# Revit family: 27435 PRESTO DL 400 E TOUCH
name_source: partatom
category: Appareils sanitaires
units: mm (PartAtom-declared; Revit-internal decimal feet)

## family parameters
Cote de connecteur circulaire = Utiliser le diamètre
Couper avec des vides une fois chargée = Non
Hôte = Mur
Numéro OmniClass = 23.45.05.14.17
Partagée = Non
Point de calcul de pièce = Non
Titre OmniClass = Showers
Toujours verticalement = Oui
Type d'élément = Normal

## types (1)
- 27435 PRESTO DL 400 E TOUCH
    Arrivée d'eau = G 3/4"
    Categorie BIM = Sanitaire
    Debit = 6-8l/min
    Description = Robinet simple sensitif pour douche en applique sans robinet d'arrêt
    Elévation par défaut = 0 mm  [stored 0 ft]
    Fabricant = LES ROBINETS PRESTO S.A.
    Famille produit = Douche
    Garantie = 3
    Groupe produit = Sensitif
    Hauteur = 1090 mm
    Longueur = 115 mm
    Materiau principal = Metal
    Materiau secondaire = Aluminum
    Modèle = 27435 PRESTO DL 400 E TOUCH
    Nom du fabricant = Presto
    Pays designer = France
    Pays fabricant = France
    Poids Net (Kg) = 0
    Product SKU = 27435
    Profondeur = 80 mm
    Temps d'ecoulement = 20-35s
    UNSPSC Code = 301815
    URL = http://www.prestodatashare.com

note: [stored X ft] marks values corroborated as IEEE doubles in the binary element streams (Revit-internal decimal feet)

## geometry (parser evidence)
native form markers: Blend x1, Sweep x6
no freeform markers — native parametric forms only
